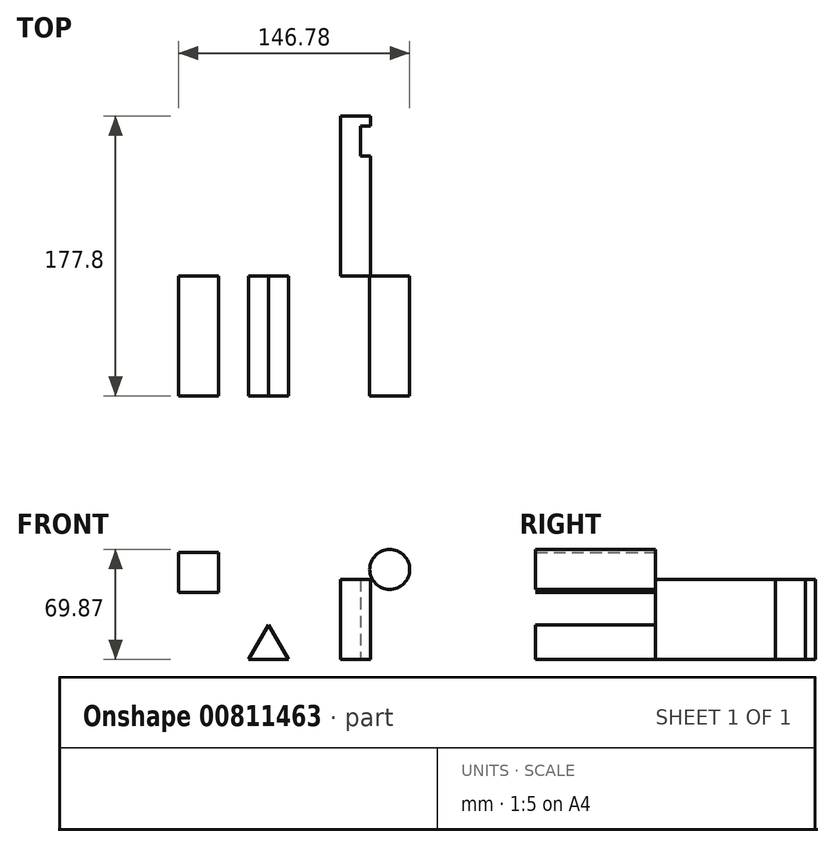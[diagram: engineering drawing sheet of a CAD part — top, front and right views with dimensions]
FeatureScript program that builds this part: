
annotation { "Feature Type Name" : "Feature", "Feature Type Description" : "" }
export const myFeature = defineFeature(function(context is Context, id is Id, definition is map)
    precondition{}
    {
        {
            var Q0;
            Q0=qCreatedBy(makeId("Front.planeOp"),FACE);
            var sketch = newSketch(context, id + "F0", { "sketchPlane" : qUnion([Q0])});
            skLineSegment(sketch, "E0", {"start": v(-87.92, 67.92) * mm, "end": v(-87.92, 42.52) * mm});
            skLineSegment(sketch, "E1", {"start": v(-87.92, 42.52) * mm, "end": v(-62.52, 42.52) * mm});
            skLineSegment(sketch, "E2", {"start": v(-62.52, 42.52) * mm, "end": v(-62.52, 67.92) * mm});
            skLineSegment(sketch, "E3", {"start": v(-62.52, 67.92) * mm, "end": v(-87.92, 67.92) * mm});
            skCircle(sketch, "E4", {"center": v(46.16, 57.17) * mm, "radius": 12.7 * mm});
            skLineSegment(sketch, "E5", {"start": v(-17.95, 0) * mm, "end": v(-43.35, 0) * mm});
            skLineSegment(sketch, "E6", {"start": v(-43.35, 0) * mm, "end": v(-30.65, 22) * mm});
            skLineSegment(sketch, "E7", {"start": v(-30.65, 22) * mm, "end": v(-17.95, 0) * mm});
            skSolve(sketch);
        }
        {
            var Q0;
            Q0=makeQuery(id+"F0.imprint","IMPRINT",FACE,{"disambiguationData":[TD([[makeQuery(id+"F0.imprint","IMPRINT",EDGE,{"derivedFrom":sQuery(id+"F0.wireOp",EDGE,"WNQzDlds-mwdv-Ayye-IiQT-4eMzcdhSNTBO")}),1.0]])]});
            var Q1;
            Q1=makeQuery(id+"F0.imprint","IMPRINT",FACE,{"disambiguationData":[TD([[makeQuery(id+"F0.imprint","IMPRINT",EDGE,{"derivedFrom":sQuery(id+"F0.wireOp",EDGE,"E4")}),1.0]])]});
            var Q2;
            Q2=makeQuery(id+"F0.imprint","IMPRINT",FACE,{"disambiguationData":[TD([[makeQuery(id+"F0.imprint","IMPRINT",EDGE,{"derivedFrom":sQuery(id+"F0.wireOp",EDGE,"E0")}),1.0]])]});
            var Q3;
            Q3=makeQuery(id+"F0.imprint","IMPRINT",FACE,{"disambiguationData":[TD([[makeQuery(id+"F0.imprint","IMPRINT",EDGE,{"derivedFrom":sQuery(id+"F0.wireOp",EDGE,"E5")}),-1.0]])]});
            extrude(context, id + "F1", {"entities" : qUnion([Q0, Q1, Q2, Q3]), "depth" : 76.2 * mm, "offsetDistance" : 25.4 * mm});
        }
        {
            var Q0;
            Q0=qCreatedBy(makeId("Top.planeOp"),FACE);
            var sketch = newSketch(context, id + "F2", { "sketchPlane" : qUnion([Q0])});
            skLineSegment(sketch, "E8.bottom", {"start": v(34.05, 101.6) * mm, "end": v(15, 101.6) * mm});
            skLineSegment(sketch, "E8.top", {"start": v(34.05, 0) * mm, "end": v(15, 0) * mm});
            skLineSegment(sketch, "E8.left", {"start": v(34.05, 101.6) * mm, "end": v(34.05, 0) * mm});
            skLineSegment(sketch, "E8.right", {"start": v(15, 101.6) * mm, "end": v(15, 0) * mm});
            skLineSegment(sketch, "E9.bottom", {"start": v(34.05, 95.25) * mm, "end": v(27.7, 95.25) * mm});
            skLineSegment(sketch, "E9.top", {"start": v(34.05, 76.2) * mm, "end": v(27.7, 76.2) * mm});
            skLineSegment(sketch, "E9.left", {"start": v(34.05, 95.25) * mm, "end": v(34.05, 76.2) * mm});
            skLineSegment(sketch, "E9.right", {"start": v(27.7, 95.25) * mm, "end": v(27.7, 76.2) * mm});
            skSolve(sketch);
        }
        {
            var Q0;
            {var subQ4=sQuery(id+"F2.wireOp",EDGE,"E8.bottom");Q0=makeQuery(id+"F2.imprint","IMPRINT",FACE,{"disambiguationData":[TD([[makeQuery(id+"F2.imprint","IMPRINT",EDGE,{"derivedFrom":subQ4}),1.0]])]});}
            extrude(context, id + "F3", {"entities" : qUnion([Q0]), "operationType" : NewBodyOperationType.ADD, "depth" : 50.8 * mm, "offsetDistance" : 25.4 * mm});
        }
    });
